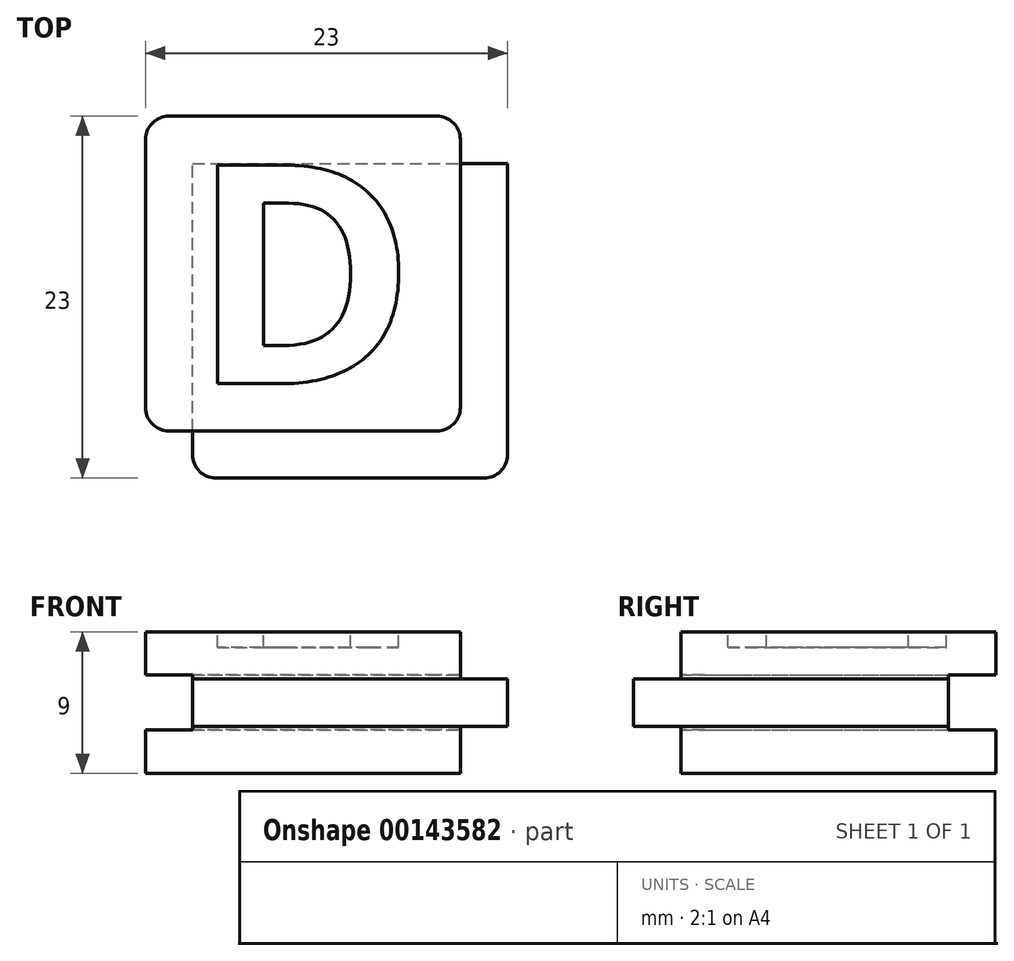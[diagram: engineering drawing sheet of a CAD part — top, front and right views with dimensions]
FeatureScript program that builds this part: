
annotation { "Feature Type Name" : "Feature", "Feature Type Description" : "" }
export const myFeature = defineFeature(function(context is Context, id is Id, definition is map)
    precondition{}
    {
        {
            var Q0;
            Q0=qCreatedBy(makeId("Front.planeOp"),FACE);
            var sketch = newSketch(context, id + "F0", { "sketchPlane" : qUnion([Q0])});
            skLineSegment(sketch, "E0.bottom", {"start": v(10, 4.5) * mm, "end": v(-10, 4.5) * mm});
            skLineSegment(sketch, "E0.top", {"start": v(10, -4.5) * mm, "end": v(-10, -4.5) * mm});
            skLineSegment(sketch, "E0.left", {"start": v(10, 4.5) * mm, "end": v(10, -4.5) * mm});
            skLineSegment(sketch, "E0.right", {"start": v(-10, 4.5) * mm, "end": v(-10, -4.5) * mm});
            skPoint(sketch, "E0.middle", {"position": v(0, 0) * mm});
            skLineSegment(sketch, "E1.bottom", {"start": v(13, 1.5) * mm, "end": v(7, 1.5) * mm});
            skLineSegment(sketch, "E1.top", {"start": v(13, -1.5) * mm, "end": v(7, -1.5) * mm});
            skLineSegment(sketch, "E1.left", {"start": v(13, 1.5) * mm, "end": v(13, -1.5) * mm});
            skLineSegment(sketch, "E1.right", {"start": v(7, 1.5) * mm, "end": v(7, -1.5) * mm});
            skPoint(sketch, "E1.middle", {"position": v(10, 0) * mm});
            skLineSegment(sketch, "E2.bottom", {"start": v(7, 1.5) * mm, "end": v(-7, 1.5) * mm});
            skLineSegment(sketch, "E2.top", {"start": v(7, -1.5) * mm, "end": v(-7, -1.5) * mm});
            skLineSegment(sketch, "E2.right", {"start": v(-7, 1.5) * mm, "end": v(-7, -1.5) * mm});
            skLineSegment(sketch, "E3.bottom", {"start": v(-7, -1.5) * mm, "end": v(-10, -1.5) * mm});
            skLineSegment(sketch, "E3.top", {"start": v(-7, 1.5) * mm, "end": v(-10, 1.5) * mm});
            skLineSegment(sketch, "E3.left", {"start": v(-7, -1.5) * mm, "end": v(-7, 1.5) * mm});
            skLineSegment(sketch, "E3.right", {"start": v(-10, -1.5) * mm, "end": v(-10, 1.5) * mm});
            skSolve(sketch);
        }
        {
            var Q0;
            {var subQ5=sQuery(id+"F0.wireOp",EDGE,"E0.bottom");Q0=makeQuery(id+"F0.imprint","IMPRINT",FACE,{"disambiguationData":[TD([[makeQuery(id+"F0.imprint","IMPRINT",EDGE,{"derivedFrom":subQ5}),1.0]])]});}
            var Q1;
            Q1=makeQuery(id+"F0.imprint","IMPRINT",FACE,{"disambiguationData":[TD([[makeQuery(id+"F0.imprint","IMPRINT",EDGE,{"derivedFrom":sQuery(id+"F0.wireOp",EDGE,"E2.bottom")}),1.0]])]});
            var Q2;
            {var subQ5=sQuery(id+"F0.wireOp",EDGE,"E1.left");Q2=makeQuery(id+"F0.imprint","IMPRINT",FACE,{"disambiguationData":[TD([[makeQuery(id+"F0.imprint","IMPRINT",EDGE,{"derivedFrom":subQ5}),-1.0]])]});}
            var Q3;
            {var subQ5=sQuery(id+"F0.wireOp",EDGE,"E1.right");Q3=makeQuery(id+"F0.imprint","IMPRINT",FACE,{"disambiguationData":[TD([[makeQuery(id+"F0.imprint","IMPRINT",EDGE,{"derivedFrom":subQ5}),1.0]])]});}
            var Q4;
            Q4=makeQuery(id+"F0.imprint","IMPRINT",FACE,{"disambiguationData":[TD([[makeQuery(id+"F0.imprint","IMPRINT",EDGE,{"derivedFrom":sQuery(id+"F0.wireOp",EDGE,"E3.bottom")}),-1.0]])]});
            var Q5;
            {var subQ5=sQuery(id+"F0.wireOp",EDGE,"E0.top");Q5=makeQuery(id+"F0.imprint","IMPRINT",FACE,{"disambiguationData":[TD([[makeQuery(id+"F0.imprint","IMPRINT",EDGE,{"derivedFrom":subQ5}),-1.0]])]});}
            extrude(context, id + "F1", {"entities" : qUnion([Q0, Q1, Q2, Q3, Q4, Q5]), "oppositeDirection" : true, "depth" : 20 * mm});
        }
        {
            var Q0;
            Q0=makeQuery(id+"F0.imprint","IMPRINT",FACE,{"disambiguationData":[TD([[makeQuery(id+"F0.imprint","IMPRINT",EDGE,{"derivedFrom":sQuery(id+"F0.wireOp",EDGE,"E3.bottom")}),-1.0]])]});
            var Q1;
            Q1=makeQuery(id+"F0.imprint","IMPRINT",FACE,{"disambiguationData":[TD([[makeQuery(id+"F0.imprint","IMPRINT",EDGE,{"derivedFrom":sQuery(id+"F0.wireOp",EDGE,"E2.bottom")}),1.0]])]});
            var Q2;
            {var subQ5=sQuery(id+"F0.wireOp",EDGE,"E1.right");Q2=makeQuery(id+"F0.imprint","IMPRINT",FACE,{"disambiguationData":[TD([[makeQuery(id+"F0.imprint","IMPRINT",EDGE,{"derivedFrom":subQ5}),1.0]])]});}
            var Q3;
            {var subQ5=sQuery(id+"F0.wireOp",EDGE,"E1.left");Q3=makeQuery(id+"F0.imprint","IMPRINT",FACE,{"disambiguationData":[TD([[makeQuery(id+"F0.imprint","IMPRINT",EDGE,{"derivedFrom":subQ5}),-1.0]])]});}
            extrude(context, id + "F2", {"entities" : qUnion([Q0, Q1, Q2, Q3]), "operationType" : NewBodyOperationType.ADD, "depth" : 3 * mm});
        }
        {
            var Q0;
            {var subQ0=sQuery(id+"F0.wireOp",EDGE,"E1.left");Q0=makeQuery(id+"F2.boolean.opBoolean","MERGE",FACE,{"derivedFrom":[makeQuery(id+"F1.opExtrude","SWEPT_FACE",FACE,{"disambiguationData":[OSD([subQ0])]}),makeQuery(id+"F2.opExtrude","SWEPT_FACE",FACE,{"disambiguationData":[OSD([subQ0])]})]});}
            var sketch = newSketch(context, id + "F3", { "sketchPlane" : qUnion([Q0])});
            skLineSegment(sketch, "E4.bottom", {"start": v(23, 1.75) * mm, "end": v(17, 1.75) * mm});
            skLineSegment(sketch, "E4.top", {"start": v(23, -1.75) * mm, "end": v(17, -1.75) * mm});
            skLineSegment(sketch, "E4.left", {"start": v(23, 1.75) * mm, "end": v(23, -1.75) * mm});
            skLineSegment(sketch, "E4.right", {"start": v(17, 1.75) * mm, "end": v(17, -1.75) * mm});
            skPoint(sketch, "E4.middle", {"position": v(20, 0) * mm});
            skSolve(sketch);
        }
        {
            var Q0;
            {var subQ1=sQuery(id+"F3.wireOp",EDGE,"E4.bottom");Q0=makeQuery(id+"F3.imprint","IMPRINT",FACE,{"disambiguationData":[TD([[makeQuery(id+"F3.imprint","IMPRINT",EDGE,{"derivedFrom":subQ1}),1.0]])]});}
            var Q1;
            {var subQ1=sQuery(id+"F0.wireOp",EDGE,"E1.left");var subQ8=makeQuery(id+"F1.opExtrude","CAP_EDGE",EDGE,{"disambiguationData":[OSD([subQ1])],"isStart":false});Q1=makeQuery(id+"F3.imprint","IMPRINT",FACE,{"disambiguationData":[TD([[makeQuery(id+"F3.imprint","IMPRINT",EDGE,{"derivedFrom":subQ8}),-1.0]])]});}
            extrude(context, id + "F4", {"entities" : qUnion([Q0, Q1]), "operationType" : NewBodyOperationType.REMOVE, "oppositeDirection" : true, "depth" : 100 * mm});
        }
        {
            var Q0;
            Q0=makeQuery(id+"F4.boolean.opBoolean","COPY",FACE,{"derivedFrom":makeQuery(id+"F4.opExtrude","SWEPT_FACE",FACE,{"disambiguationData":[OSD([sQuery(id+"F3.wireOp",EDGE,"E4.right")])]})});
            var sketch = newSketch(context, id + "F5", { "sketchPlane" : qUnion([Q0])});
            skLineSegment(sketch, "E5.bottom", {"start": v(13, 1.75) * mm, "end": v(7, 1.75) * mm});
            skLineSegment(sketch, "E5.top", {"start": v(13, -1.75) * mm, "end": v(7, -1.75) * mm});
            skLineSegment(sketch, "E5.left", {"start": v(13, 1.75) * mm, "end": v(13, -1.75) * mm});
            skLineSegment(sketch, "E5.right", {"start": v(7, 1.75) * mm, "end": v(7, -1.75) * mm});
            skPoint(sketch, "E5.middle", {"position": v(10, 0) * mm});
            skSolve(sketch);
        }
        {
            var Q0;
            {var subQ3=sQuery(id+"F5.wireOp",EDGE,"E5.left");Q0=makeQuery(id+"F5.imprint","IMPRINT",FACE,{"disambiguationData":[TD([[makeQuery(id+"F5.imprint","IMPRINT",EDGE,{"derivedFrom":subQ3}),-1.0]])]});}
            var Q1;
            {var subQ4=sQuery(id+"F5.wireOp",EDGE,"E5.right");Q1=makeQuery(id+"F5.imprint","IMPRINT",FACE,{"disambiguationData":[TD([[makeQuery(id+"F5.imprint","IMPRINT",EDGE,{"derivedFrom":subQ4}),1.0]])]});}
            extrude(context, id + "F6", {"entities" : qUnion([Q0, Q1]), "operationType" : NewBodyOperationType.REMOVE, "oppositeDirection" : true, "depth" : 100 * mm});
        }
        {
            var Q0;
            Q0=makeQuery(id+"F6.boolean.opBoolean","INTERSECT",EDGE,{"derivedFrom":[makeQuery(id+"F2.opExtrude","CAP_FACE",FACE,{"disambiguationData":[OSD([sQuery(id+"F0.wireOp",EDGE,"E1.bottom"),sQuery(id+"F0.wireOp",EDGE,"E1.top"),sQuery(id+"F0.wireOp",EDGE,"E1.left"),sQuery(id+"F0.wireOp",EDGE,"E2.bottom"),sQuery(id+"F0.wireOp",EDGE,"E2.top"),sQuery(id+"F0.wireOp",EDGE,"E3.bottom"),sQuery(id+"F0.wireOp",EDGE,"E3.top"),sQuery(id+"F0.wireOp",EDGE,"E3.right")])],"isStart":false}),makeQuery(id+"F6.opExtrude","SWEPT_FACE",FACE,{"disambiguationData":[OSD([sQuery(id+"F5.wireOp",EDGE,"E5.right")])]})]});
            var Q1;
            Q1=makeQuery(id+"F2.opExtrude","CAP_EDGE",EDGE,{"disambiguationData":[OSD([sQuery(id+"F0.wireOp",EDGE,"E1.left")])],"isStart":false});
            var Q2;
            {var subQ0=sQuery(id+"F0.wireOp",EDGE,"E0.left");Q2=makeQuery(id+"F1.opExtrude","CAP_EDGE",EDGE,{"disambiguationData":[OSD([subQ0]),TDD([makeQuery(id+"F0.imprint","IMPRINT",EDGE,{"disambiguationData":[TD([[makeQuery(id+"F0.imprint","INTERSECT",VERTEX,{"derivedFrom":[sQuery(id+"F0.wireOp",EDGE,"E0.bottom"),subQ0]}),-1.0]])],"derivedFrom":subQ0})])],"isStart":true});}
            var Q3;
            {var subQ0=sQuery(id+"F0.wireOp",EDGE,"E0.left");Q3=makeQuery(id+"F1.opExtrude","CAP_EDGE",EDGE,{"disambiguationData":[OSD([subQ0]),TDD([makeQuery(id+"F0.imprint","IMPRINT",EDGE,{"disambiguationData":[TD([[makeQuery(id+"F0.imprint","INTERSECT",VERTEX,{"derivedFrom":[sQuery(id+"F0.wireOp",EDGE,"E0.top"),subQ0]}),1.0]])],"derivedFrom":subQ0})])],"isStart":true});}
            var Q4;
            {var subQ0=sQuery(id+"F0.wireOp",EDGE,"E3.right");var subQ1=sQuery(id+"F0.wireOp",EDGE,"E0.right");var subQ3=sQuery(id+"F0.wireOp",EDGE,"E0.top");Q4=makeQuery(id+"F2.boolean.opBoolean","SPLIT",EDGE,{"disambiguationData":[TD([makeQuery(id+"F1.opExtrude","SWEPT_FACE",FACE,{"disambiguationData":[OSD([subQ3])]})])],"derivedFrom":makeQuery(id+"F1.opExtrude","CAP_EDGE",EDGE,{"disambiguationData":[OSD([subQ1,subQ0])],"isStart":true})});}
            var Q5;
            {var subQ1=sQuery(id+"F0.wireOp",EDGE,"E3.right");var subQ2=sQuery(id+"F0.wireOp",EDGE,"E0.right");var subQ3=sQuery(id+"F0.wireOp",EDGE,"E0.bottom");Q5=makeQuery(id+"F2.boolean.opBoolean","SPLIT",EDGE,{"disambiguationData":[TD([makeQuery(id+"F1.opExtrude","SWEPT_FACE",FACE,{"disambiguationData":[OSD([subQ3])]})])],"derivedFrom":makeQuery(id+"F1.opExtrude","CAP_EDGE",EDGE,{"disambiguationData":[OSD([subQ2,subQ1])],"isStart":true})});}
            var Q6;
            Q6=makeQuery(id+"F6.boolean.opBoolean","COPY",EDGE,{"derivedFrom":makeQuery(id+"F6.opExtrude","CAP_EDGE",EDGE,{"disambiguationData":[OSD([sQuery(id+"F5.wireOp",EDGE,"E5.right")])],"isStart":true})});
            var Q7;
            {var subQ0=sQuery(id+"F0.wireOp",EDGE,"E3.right");var subQ1=sQuery(id+"F0.wireOp",EDGE,"E0.right");var subQ2=sQuery(id+"F0.wireOp",EDGE,"E0.bottom");Q7=makeQuery(id+"F4.boolean.opBoolean","SPLIT",EDGE,{"disambiguationData":[TD([makeQuery(id+"F1.opExtrude","SWEPT_FACE",FACE,{"disambiguationData":[OSD([subQ2])]})])],"derivedFrom":makeQuery(id+"F1.opExtrude","CAP_EDGE",EDGE,{"disambiguationData":[OSD([subQ1,subQ0])],"isStart":false})});}
            var Q8;
            {var subQ0=sQuery(id+"F0.wireOp",EDGE,"E3.right");var subQ1=sQuery(id+"F0.wireOp",EDGE,"E0.right");var subQ2=sQuery(id+"F0.wireOp",EDGE,"E0.top");Q8=makeQuery(id+"F4.boolean.opBoolean","SPLIT",EDGE,{"disambiguationData":[TD([makeQuery(id+"F1.opExtrude","SWEPT_FACE",FACE,{"disambiguationData":[OSD([subQ2])]})])],"derivedFrom":makeQuery(id+"F1.opExtrude","CAP_EDGE",EDGE,{"disambiguationData":[OSD([subQ1,subQ0])],"isStart":false})});}
            var Q9;
            Q9=makeQuery(id+"F4.boolean.opBoolean","COPY",EDGE,{"derivedFrom":makeQuery(id+"F4.opExtrude","CAP_EDGE",EDGE,{"disambiguationData":[OSD([sQuery(id+"F3.wireOp",EDGE,"E4.right")])],"isStart":true})});
            var Q10;
            {var subQ0=sQuery(id+"F0.wireOp",EDGE,"E0.left");Q10=makeQuery(id+"F1.opExtrude","CAP_EDGE",EDGE,{"disambiguationData":[OSD([subQ0]),TDD([makeQuery(id+"F0.imprint","IMPRINT",EDGE,{"disambiguationData":[TD([[makeQuery(id+"F0.imprint","INTERSECT",VERTEX,{"derivedFrom":[sQuery(id+"F0.wireOp",EDGE,"E0.bottom"),subQ0]}),-1.0]])],"derivedFrom":subQ0})])],"isStart":false});}
            var Q11;
            {var subQ0=sQuery(id+"F0.wireOp",EDGE,"E0.left");Q11=makeQuery(id+"F1.opExtrude","CAP_EDGE",EDGE,{"disambiguationData":[OSD([subQ0]),TDD([makeQuery(id+"F0.imprint","IMPRINT",EDGE,{"disambiguationData":[TD([[makeQuery(id+"F0.imprint","INTERSECT",VERTEX,{"derivedFrom":[sQuery(id+"F0.wireOp",EDGE,"E0.top"),subQ0]}),1.0]])],"derivedFrom":subQ0})])],"isStart":false});}
            fillet(context, id + "F7", {"entities" : qUnion([Q0, Q1, Q2, Q3, Q4, Q5, Q6, Q7, Q8, Q9, Q10, Q11]), "radius" : 1.5 * mm, "tangentPropagation" : true, "allowEdgeOverflow" : false});
        }
        {
            var Q0;
            Q0=makeQuery(id+"F1.opExtrude","SWEPT_FACE",FACE,{"disambiguationData":[OSD([sQuery(id+"F0.wireOp",EDGE,"E0.bottom")])]});
            var sketch = newSketch(context, id + "F8", { "sketchPlane" : qUnion([Q0])});
            skText(sketch, "E6", { "text": "D", "fontName": "OpenSans-Bold.ttf"});
            skLineSegment(sketch, "E7.0", {"start": v(11.23, 3) * mm, "end": v(-11.07, 3) * mm});
            const initialGuessF8  = {"E6": [-0.00718, 0.003, 1, 0, 0.014]};
            skSetInitialGuess(sketch, initialGuessF8);
            skSolve(sketch);
        }
        {
            var Q0;
            Q0=makeQuery(id+"F8.imprint","IMPRINT",FACE,{"disambiguationData":[TD([[makeQuery(id+"F8.imprint","IMPRINT",EDGE,{"derivedFrom":sQuery(id+"F8.wireOp",EDGE,"E6.sketch_text.stroke-0")}),-1.0]])]});
            extrude(context, id + "F9", {"entities" : qUnion([Q0]), "operationType" : NewBodyOperationType.REMOVE, "oppositeDirection" : true, "depth" : 1 * mm});
        }
    });
